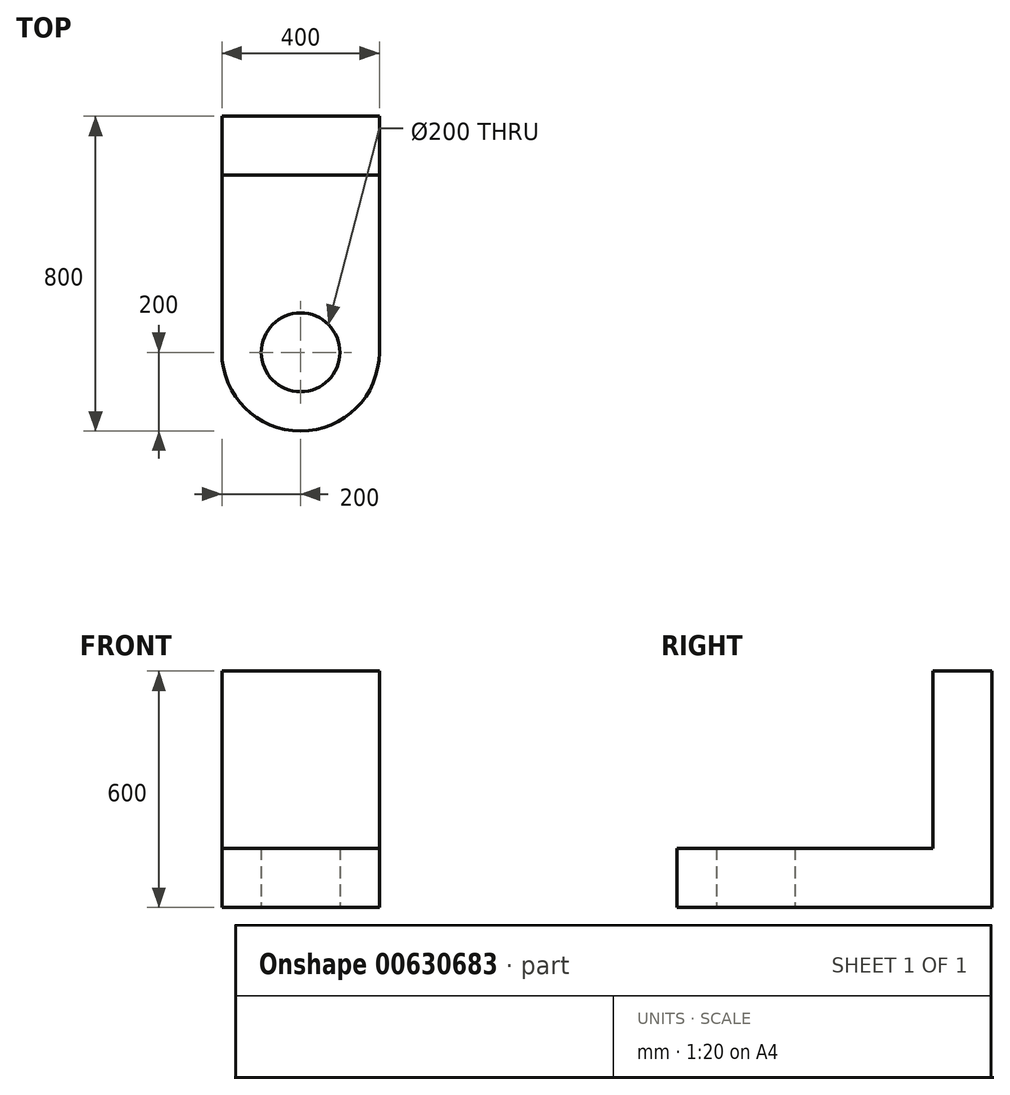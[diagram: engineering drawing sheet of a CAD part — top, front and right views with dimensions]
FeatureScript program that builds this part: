
annotation { "Feature Type Name" : "Feature", "Feature Type Description" : "" }
export const myFeature = defineFeature(function(context is Context, id is Id, definition is map)
    precondition{}
    {
        {
            var Q0;
            Q0=qCreatedBy(makeId("Top.planeOp"),FACE);
            var sketch = newSketch(context, id + "F0", { "sketchPlane" : qUnion([Q0])});
            skLineSegment(sketch, "E0.bottom", {"start": v(-200, -300) * mm, "end": v(200, -300) * mm});
            skLineSegment(sketch, "E0.top", {"start": v(-200, 300) * mm, "end": v(200, 300) * mm});
            skLineSegment(sketch, "E0.left", {"start": v(-200, -300) * mm, "end": v(-200, 300) * mm});
            skLineSegment(sketch, "E0.right", {"start": v(200, -300) * mm, "end": v(200, 300) * mm});
            skPoint(sketch, "E0.middle", {"position": v(0, 0) * mm});
            skArc(sketch, "E1", {"start": v(-200, -300) * mm, "mid": v(0, -500) * mm, "end": v(200, -300) * mm});
            skCircle(sketch, "E2", {"center": v(0, -300) * mm, "radius": 100 * mm});
            skSolve(sketch);
        }
        {
            var Q0;
            Q0 = qSketchRegion(id + "F0", true);
            extrude(context, id + "F1", {"entities" : qUnion([Q0]), "depth" : 150 * mm, "offsetDistance" : 25 * mm});
        }
        {
            var Q0;
            Q0=makeQuery(id+"F1.opExtrude","CAP_FACE",FACE,{"disambiguationData":[OSD([sQuery(id+"F0.wireOp",EDGE,"E0.top"),sQuery(id+"F0.wireOp",EDGE,"E0.left"),sQuery(id+"F0.wireOp",EDGE,"E0.right"),sQuery(id+"F0.wireOp",EDGE,"E1"),sQuery(id+"F0.wireOp",EDGE,"E2")])],"isStart":false});
            var sketch = newSketch(context, id + "F2", { "sketchPlane" : qUnion([Q0])});
            skLineSegment(sketch, "E3.bottom", {"start": v(-200, 300) * mm, "end": v(200, 300) * mm});
            skLineSegment(sketch, "E3.top", {"start": v(-200, 150) * mm, "end": v(200, 150) * mm});
            skLineSegment(sketch, "E3.left", {"start": v(-200, 300) * mm, "end": v(-200, 150) * mm});
            skLineSegment(sketch, "E3.right", {"start": v(200, 300) * mm, "end": v(200, 150) * mm});
            skPoint(sketch, "E3.middle", {"position": v(0, 225) * mm});
            skSolve(sketch);
        }
        {
            var Q0;
            Q0 = qSketchRegion(id + "F2", true);
            extrude(context, id + "F3", {"entities" : qUnion([Q0]), "operationType" : NewBodyOperationType.ADD, "depth" : 450 * mm, "offsetDistance" : 25 * mm});
        }
    });
